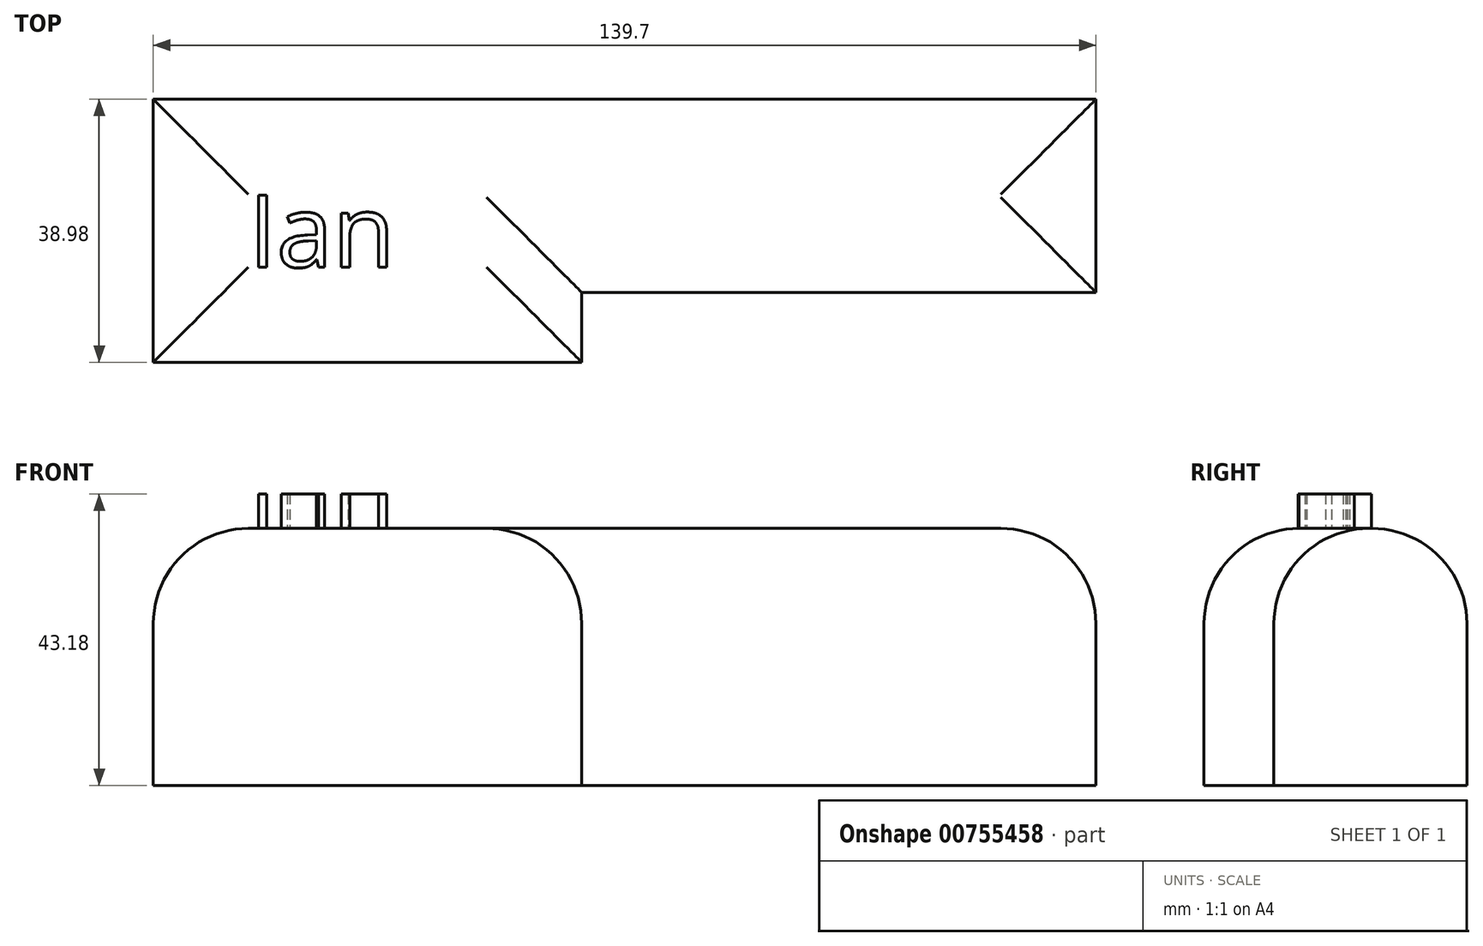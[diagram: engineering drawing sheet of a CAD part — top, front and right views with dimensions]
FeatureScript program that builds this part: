
annotation { "Feature Type Name" : "Feature", "Feature Type Description" : "" }
export const myFeature = defineFeature(function(context is Context, id is Id, definition is map)
    precondition{}
    {
        {
            var Q0;
            Q0=qCreatedBy(makeId("Top.planeOp"),FACE);
            var sketch = newSketch(context, id + "F0", { "sketchPlane" : qUnion([Q0])});
            skLineSegment(sketch, "E0.bottom", {"start": v(76.2, -28.62) * mm, "end": v(0, -28.62) * mm});
            skLineSegment(sketch, "E0.top", {"start": v(76.2, 0) * mm, "end": v(0, 0) * mm});
            skLineSegment(sketch, "E0.left", {"start": v(76.2, -28.62) * mm, "end": v(76.2, 0) * mm});
            skLineSegment(sketch, "E0.right", {"start": v(0, -28.62) * mm, "end": v(0, 0) * mm});
            skLineSegment(sketch, "E1.bottom", {"start": v(0, 0) * mm, "end": v(-63.5, 0) * mm});
            skLineSegment(sketch, "E1.top", {"start": v(0, -38.98) * mm, "end": v(-63.5, -38.98) * mm});
            skLineSegment(sketch, "E1.left", {"start": v(0, 0) * mm, "end": v(0, -38.98) * mm});
            skLineSegment(sketch, "E1.right", {"start": v(-63.5, 0) * mm, "end": v(-63.5, -38.98) * mm});
            skSolve(sketch);
        }
        {
            var Q0;
            Q0 = qSketchRegion(id + "F0", true);
            extrude(context, id + "F1", {"entities" : qUnion([Q0]), "depth" : 38.1 * mm, "offsetDistance" : 25.4 * mm});
        }
        {
            var Q0;
            Q0=makeQuery(id+"F1.opExtrude","CAP_EDGE",EDGE,{"disambiguationData":[OSD([sQuery(id+"F0.wireOp",EDGE,"E0.top"),sQuery(id+"F0.wireOp",EDGE,"E1.bottom")])],"isStart":false});
            var Q1;
            Q1=makeQuery(id+"F1.opExtrude","CAP_EDGE",EDGE,{"disambiguationData":[OSD([sQuery(id+"F0.wireOp",EDGE,"E1.right")])],"isStart":false});
            var Q2;
            Q2=makeQuery(id+"F1.opExtrude","CAP_EDGE",EDGE,{"disambiguationData":[OSD([sQuery(id+"F0.wireOp",EDGE,"E1.top")])],"isStart":false});
            var Q3;
            Q3=makeQuery(id+"F1.opExtrude","CAP_FACE",FACE,{"disambiguationData":[OSD([sQuery(id+"F0.wireOp",EDGE,"E0.bottom"),sQuery(id+"F0.wireOp",EDGE,"E0.top"),sQuery(id+"F0.wireOp",EDGE,"E0.left"),sQuery(id+"F0.wireOp",EDGE,"E1.bottom"),sQuery(id+"F0.wireOp",EDGE,"E1.top"),sQuery(id+"F0.wireOp",EDGE,"E1.left"),sQuery(id+"F0.wireOp",EDGE,"E1.right")])],"isStart":false});
            fillet(context, id + "F2", {"entities" : qUnion([Q0, Q1, Q2, Q3]), "radius" : 14.1 * mm, "tangentPropagation" : true, "allowEdgeOverflow" : false});
        }
        {
            var Q0;
            Q0=makeQuery(id+"F1.opExtrude","CAP_FACE",FACE,{"disambiguationData":[OSD([sQuery(id+"F0.wireOp",EDGE,"E0.bottom"),sQuery(id+"F0.wireOp",EDGE,"E0.top"),sQuery(id+"F0.wireOp",EDGE,"E0.left"),sQuery(id+"F0.wireOp",EDGE,"E1.bottom"),sQuery(id+"F0.wireOp",EDGE,"E1.top"),sQuery(id+"F0.wireOp",EDGE,"E1.left"),sQuery(id+"F0.wireOp",EDGE,"E1.right")])],"isStart":false});
            var sketch = newSketch(context, id + "F3", { "sketchPlane" : qUnion([Q0])});
            skText(sketch, "E2", { "text": "Ian", "fontName": "OpenSans-Regular.ttf"});
            const initialGuessF3  = {"E2": [-0.0494, -0.02488, 1, 0, 0.01078]};
            skSetInitialGuess(sketch, initialGuessF3);
            skSolve(sketch);
        }
        {
            var Q0;
            Q0 = qSketchRegion(id + "F3", true);
            extrude(context, id + "F4", {"entities" : qUnion([Q0]), "operationType" : NewBodyOperationType.ADD, "depth" : 5.08 * mm, "offsetDistance" : 25.4 * mm});
        }
    });
